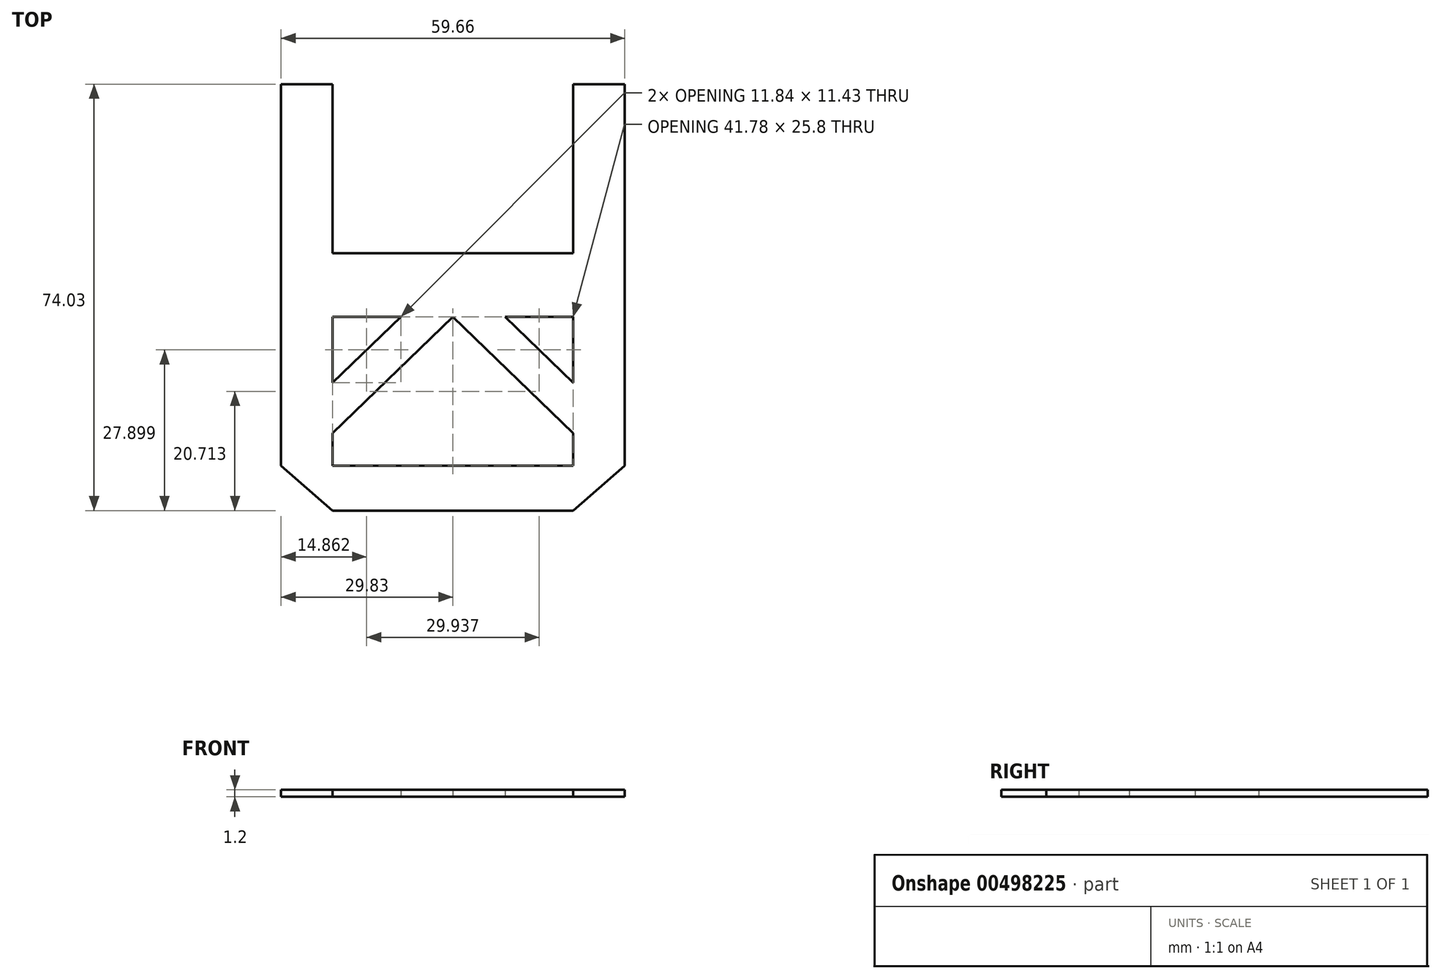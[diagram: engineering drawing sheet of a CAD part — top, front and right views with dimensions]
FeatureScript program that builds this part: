
annotation { "Feature Type Name" : "Feature", "Feature Type Description" : "" }
export const myFeature = defineFeature(function(context is Context, id is Id, definition is map)
    precondition{}
    {
        {
            var Q0;
            Q0=qCreatedBy(makeId("Top.planeOp"),FACE);
            var sketch = newSketch(context, id + "F0", { "sketchPlane" : qUnion([Q0])});
            skLineSegment(sketch, "E0", {"start": v(-20.89, -36.88) * mm, "end": v(20.89, -36.88) * mm});
            skLineSegment(sketch, "E1", {"start": v(20.89, -36.88) * mm, "end": v(20.89, 0) * mm});
            skLineSegment(sketch, "E2", {"start": v(20.89, 0) * mm, "end": v(20.89, 29.34) * mm});
            skLineSegment(sketch, "E3", {"start": v(-20.89, -36.88) * mm, "end": v(-20.89, 0) * mm});
            skLineSegment(sketch, "E4", {"start": v(-20.89, 0) * mm, "end": v(-20.89, 29.34) * mm});
            skLineSegment(sketch, "E5", {"start": v(-20.89, 0) * mm, "end": v(20.89, 0) * mm});
            skLineSegment(sketch, "E6", {"start": v(20.89, -11.08) * mm, "end": v(-20.89, -11.08) * mm});
            skLineSegment(sketch, "E7", {"start": v(-20.89, -22.5) * mm, "end": v(-9.05, -11.08) * mm});
            skLineSegment(sketch, "E8", {"start": v(-9.05, -11.08) * mm, "end": v(0, -11.08) * mm});
            skLineSegment(sketch, "E9", {"start": v(0, -11.08) * mm, "end": v(-20.89, -31.24) * mm});
            skLineSegment(sketch, "E10.MirrorCS", {"start": v(20.89, -22.5) * mm, "end": v(9.05, -11.08) * mm});
            skLineSegment(sketch, "E11.MirrorCS", {"start": v(0, -11.08) * mm, "end": v(20.89, -31.24) * mm});
            skLineSegment(sketch, "E12", {"start": v(-20.89, 29.34) * mm, "end": v(-29.83, 29.34) * mm});
            skLineSegment(sketch, "E13", {"start": v(-29.83, 29.34) * mm, "end": v(-29.83, -36.88) * mm});
            skLineSegment(sketch, "E14", {"start": v(-29.83, -36.88) * mm, "end": v(-20.89, -44.7) * mm});
            skLineSegment(sketch, "E15", {"start": v(-20.89, -44.7) * mm, "end": v(0, -44.7) * mm});
            skLineSegment(sketch, "E16.MirrorCS", {"start": v(29.83, 29.34) * mm, "end": v(29.83, -36.88) * mm});
            skLineSegment(sketch, "E17.MirrorCS", {"start": v(29.83, -36.88) * mm, "end": v(20.89, -44.7) * mm});
            skLineSegment(sketch, "E18.MirrorCS", {"start": v(20.89, -44.7) * mm, "end": v(0, -44.7) * mm});
            skLineSegment(sketch, "E19.MirrorCS", {"start": v(20.89, 29.34) * mm, "end": v(29.83, 29.34) * mm});
            skSolve(sketch);
        }
        {
            var Q0;
            Q0 = qSketchRegion(id + "F0", true);
            var Q1;
            {var subQ0=sQuery(id+"F0.wireOp",EDGE,"E7");Q1=makeQuery(id+"F0.imprint","IMPRINT",FACE,{"disambiguationData":[TD([[makeQuery(id+"F0.imprint","IMPRINT",EDGE,{"derivedFrom":subQ0}),-1.0]])]});}
            var Q2;
            {var subQ0=sQuery(id+"F0.wireOp",EDGE,"E10.MirrorCS");Q2=makeQuery(id+"F0.imprint","IMPRINT",FACE,{"disambiguationData":[TD([[makeQuery(id+"F0.imprint","IMPRINT",EDGE,{"derivedFrom":subQ0}),1.0]])]});}
            extrude(context, id + "F1", {"entities" : qUnion([Q0, Q1, Q2]), "depth" : 1.2 * mm});
        }
    });
